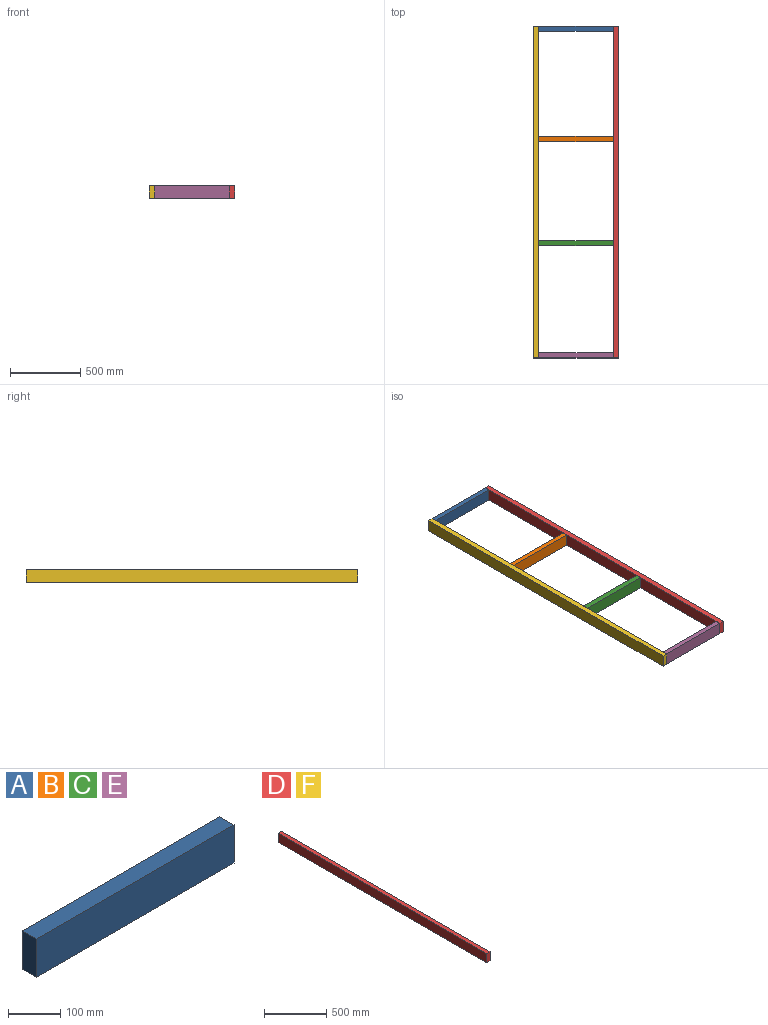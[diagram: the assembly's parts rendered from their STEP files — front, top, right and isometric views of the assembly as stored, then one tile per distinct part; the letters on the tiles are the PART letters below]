
ASSEMBLY  parts=6 mates=4
PART A: 6 faces, bbox 533.4x38.1x88.9 mm
  f0: plane 533.4x88.9mm, normal (0,1,0), area 47419.3mm2, adj f1,f3,f4,f5
  f1: plane 88.9x38.1mm, normal (-1,0,0), area 3387.1mm2, adj f0,f2,f4,f5
  f2: plane 533.4x88.9mm, normal (0,-1,0), area 47419.3mm2, adj f1,f3,f4,f5
  f3: plane 88.9x38.1mm, normal (1,0,0), area 3387.1mm2, adj f0,f2,f4,f5
  f4: plane 533.4x38.1mm, normal (0,0,1), area 20322.5mm2, adj f0,f1,f2,f3
  f5: plane 533.4x38.1mm, normal (0,0,-1), area 20322.5mm2, adj f0,f1,f2,f3
PART B: same geometry as A
PART C: same geometry as A
PART D: 6 faces, bbox 38.1x2362.2x88.9 mm
  f0: plane 2362.2x38.1mm, normal (0,0,1), area 89999.8mm2, adj f1,f3,f4,f5
  f1: plane 88.9x38.1mm, normal (0,-1,0), area 3387.1mm2, adj f0,f2,f4,f5
  f2: plane 2362.2x38.1mm, normal (0,0,-1), area 89999.8mm2, adj f1,f3,f4,f5
  f3: plane 88.9x38.1mm, normal (0,1,0), area 3387.1mm2, adj f0,f2,f4,f5
  f4: plane 2362.2x88.9mm, normal (1,0,0), area 209999.6mm2, adj f0,f1,f2,f3
  f5: plane 2362.2x88.9mm, normal (-1,0,0), area 209999.6mm2, adj f0,f1,f2,f3
PART E: same geometry as A
PART F: same geometry as D
PLACE A t=(-228.5,2491.65,84.39)mm
PLACE B t=(-228.5,1707.43,84.39)mm
PLACE C t=(-228.5,964.61,84.39)mm
PLACE D t=(304.9,129.45,173.29)mm fixed
PLACE E t=(-228.5,167.55,84.39)mm
PLACE F t=(-266.6,129.45,173.29)mm
MATE fastened A.f3 <-> B.f3  axis (1,0,0) through (304.9,2453.55,84.39)mm
MATE fastened C.f3 <-> E.f3  axis (1,0,0) through (304.9,926.51,84.39)mm
MATE fastened F.f0 <-> E.f4  axis (0,0,1) through (-228.5,129.45,173.29)mm
MATE fastened A.f4 <-> F.f0  axis (0,0,1) through (-228.5,2491.65,173.29)mm
